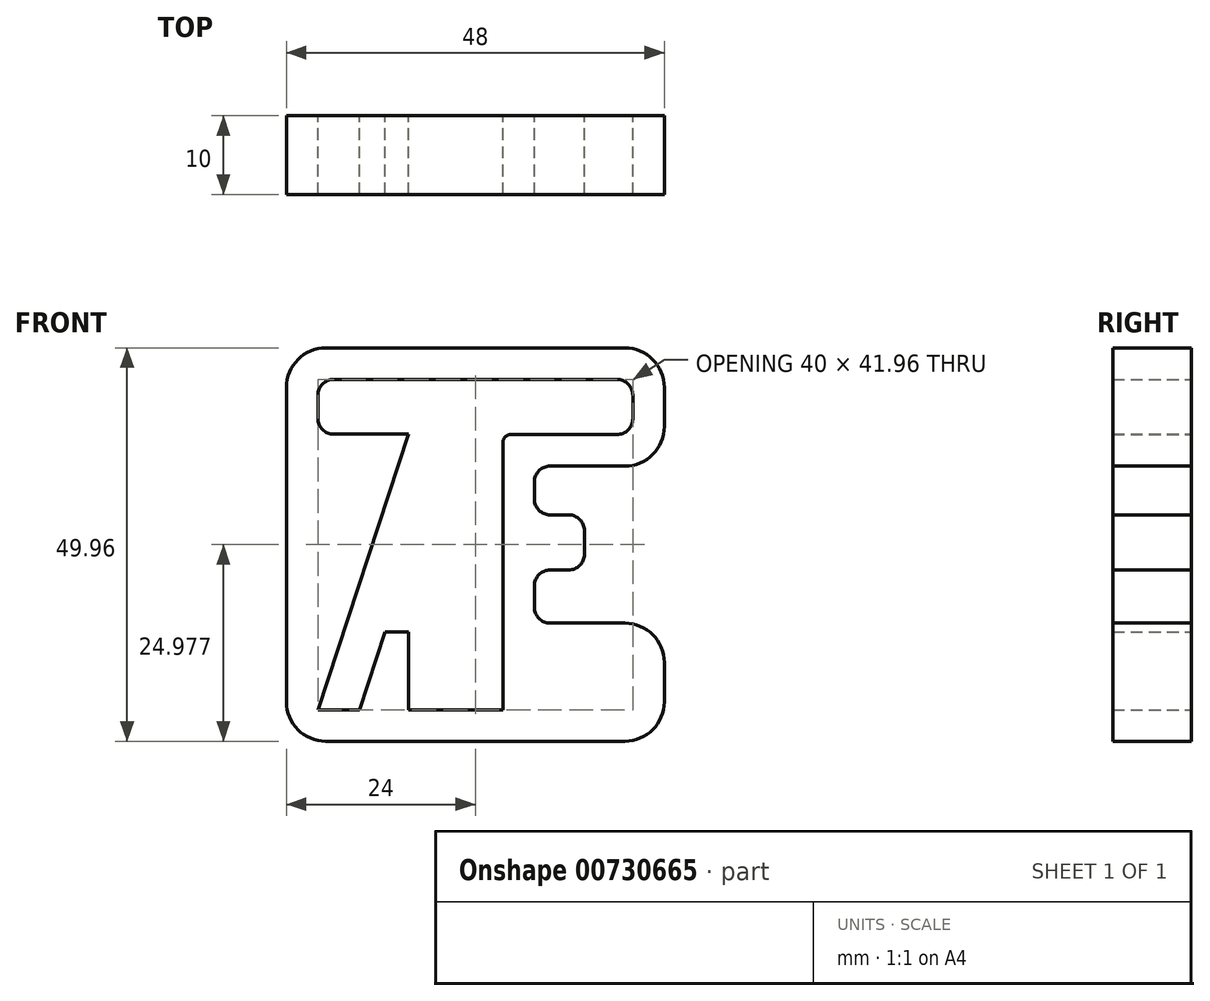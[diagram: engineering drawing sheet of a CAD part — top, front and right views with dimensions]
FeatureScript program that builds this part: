
annotation { "Feature Type Name" : "Feature", "Feature Type Description" : "" }
export const myFeature = defineFeature(function(context is Context, id is Id, definition is map)
    precondition{}
    {
        {
            var Q0;
            Q0=qCreatedBy(makeId("Front.planeOp"),FACE);
            var sketch = newSketch(context, id + "F0", { "sketchPlane" : qUnion([Q0])});
            skLineSegment(sketch, "E0", {"start": v(-5, 16.18) * mm, "end": v(-16.5, -18.82) * mm});
            skLineSegment(sketch, "E1", {"start": v(-16.5, -18.82) * mm, "end": v(-11.24, -18.82) * mm});
            skLineSegment(sketch, "E2", {"start": v(-11.24, -18.82) * mm, "end": v(-8, -8.96) * mm});
            skLineSegment(sketch, "E3", {"start": v(-8, -8.96) * mm, "end": v(-5, -8.96) * mm});
            skLineSegment(sketch, "E4", {"start": v(-5, -8.96) * mm, "end": v(-5, -18.82) * mm});
            skLineSegment(sketch, "E5", {"start": v(-5, -18.82) * mm, "end": v(0, -18.82) * mm});
            skLineSegment(sketch, "E6", {"start": v(23.5, 16.14) * mm, "end": v(23.5, 23.14) * mm});
            skLineSegment(sketch, "E7", {"start": v(23.5, 23.14) * mm, "end": v(-16.5, 23.14) * mm});
            skLineSegment(sketch, "E8", {"start": v(-16.5, 23.14) * mm, "end": v(-16.5, 16.18) * mm});
            skLineSegment(sketch, "E9", {"start": v(-16.5, 16.18) * mm, "end": v(-5, 16.18) * mm});
            skLineSegment(sketch, "E10", {"start": v(23.5, 16.14) * mm, "end": v(7, 16.14) * mm});
            skLineSegment(sketch, "E11", {"start": v(7, 16.14) * mm, "end": v(7, -18.82) * mm});
            skLineSegment(sketch, "E12", {"start": v(7, -18.82) * mm, "end": v(0, -18.82) * mm});
            skLineSegment(sketch, "E13", {"start": v(27.5, 27.14) * mm, "end": v(-20.5, 27.14) * mm});
            skLineSegment(sketch, "E14", {"start": v(-20.5, 27.14) * mm, "end": v(-20.5, -22.82) * mm});
            skLineSegment(sketch, "E15", {"start": v(-20.5, -22.82) * mm, "end": v(27.5, -22.82) * mm});
            skLineSegment(sketch, "E16", {"start": v(27.5, -22.82) * mm, "end": v(27.5, -7.82) * mm});
            skLineSegment(sketch, "E17", {"start": v(27.5, -7.82) * mm, "end": v(11, -7.82) * mm});
            skLineSegment(sketch, "E18", {"start": v(11, -7.82) * mm, "end": v(11, -1.07) * mm});
            skLineSegment(sketch, "E19", {"start": v(11, -1.07) * mm, "end": v(17.35, -1.07) * mm});
            skLineSegment(sketch, "E20", {"start": v(17.35, -1.07) * mm, "end": v(17.35, 5.93) * mm});
            skLineSegment(sketch, "E21", {"start": v(17.35, 5.93) * mm, "end": v(11, 5.93) * mm});
            skLineSegment(sketch, "E22", {"start": v(11, 5.93) * mm, "end": v(11, 12.14) * mm});
            skLineSegment(sketch, "E23", {"start": v(11, 12.14) * mm, "end": v(27.5, 12.14) * mm});
            skLineSegment(sketch, "E24", {"start": v(27.5, 12.14) * mm, "end": v(27.5, 27.14) * mm});
            skSolve(sketch);
        }
        {
            var Q0;
            Q0=qSketchRegion(id+"F0",true);
            extrude(context, id + "F1", {"entities" : qUnion([Q0]), "depth" : 10 * mm, "offsetDistance" : 25 * mm});
        }
        {
            var Q0;
            Q0=makeQuery(id+"F1.opExtrude","SWEPT_EDGE",EDGE,{"disambiguationData":[OSD([sQuery(id+"F0.wireOp",EDGE,"E7"),sQuery(id+"F0.wireOp",EDGE,"E8")])]});
            var Q1;
            Q1=makeQuery(id+"F1.opExtrude","SWEPT_EDGE",EDGE,{"disambiguationData":[OSD([sQuery(id+"F0.wireOp",EDGE,"E8"),sQuery(id+"F0.wireOp",EDGE,"E9")])]});
            var Q2;
            Q2=makeQuery(id+"F1.opExtrude","SWEPT_EDGE",EDGE,{"disambiguationData":[OSD([sQuery(id+"F0.wireOp",EDGE,"E6"),sQuery(id+"F0.wireOp",EDGE,"E7")])]});
            var Q3;
            Q3=makeQuery(id+"F1.opExtrude","SWEPT_EDGE",EDGE,{"disambiguationData":[OSD([sQuery(id+"F0.wireOp",EDGE,"E6"),sQuery(id+"F0.wireOp",EDGE,"E10")])]});
            fillet(context, id + "F2", {"entities" : qUnion([Q0, Q1, Q2, Q3]), "radius" : 2 * mm, "tangentPropagation" : true, "allowEdgeOverflow" : false});
        }
        {
            var Q0;
            Q0=makeQuery(id+"F1.opExtrude","SWEPT_EDGE",EDGE,{"disambiguationData":[OSD([sQuery(id+"F0.wireOp",EDGE,"E13"),sQuery(id+"F0.wireOp",EDGE,"E14")])]});
            var Q1;
            Q1=makeQuery(id+"F1.opExtrude","SWEPT_EDGE",EDGE,{"disambiguationData":[OSD([sQuery(id+"F0.wireOp",EDGE,"E13"),sQuery(id+"F0.wireOp",EDGE,"E24")])]});
            var Q2;
            Q2=makeQuery(id+"F1.opExtrude","SWEPT_EDGE",EDGE,{"disambiguationData":[OSD([sQuery(id+"F0.wireOp",EDGE,"E23"),sQuery(id+"F0.wireOp",EDGE,"E24")])]});
            var Q3;
            Q3=makeQuery(id+"F1.opExtrude","SWEPT_EDGE",EDGE,{"disambiguationData":[OSD([sQuery(id+"F0.wireOp",EDGE,"E14"),sQuery(id+"F0.wireOp",EDGE,"E15")])]});
            var Q4;
            Q4=makeQuery(id+"F1.opExtrude","SWEPT_EDGE",EDGE,{"disambiguationData":[OSD([sQuery(id+"F0.wireOp",EDGE,"E15"),sQuery(id+"F0.wireOp",EDGE,"E16")])]});
            var Q5;
            Q5=makeQuery(id+"F1.opExtrude","SWEPT_EDGE",EDGE,{"disambiguationData":[OSD([sQuery(id+"F0.wireOp",EDGE,"E16"),sQuery(id+"F0.wireOp",EDGE,"E17")])]});
            fillet(context, id + "F3", {"entities" : qUnion([Q0, Q1, Q2, Q3, Q4, Q5]), "radius" : 5 * mm, "tangentPropagation" : true, "allowEdgeOverflow" : false});
        }
        {
            var Q0;
            Q0=makeQuery(id+"F1.opExtrude","SWEPT_EDGE",EDGE,{"disambiguationData":[OSD([sQuery(id+"F0.wireOp",EDGE,"E22"),sQuery(id+"F0.wireOp",EDGE,"E23")])]});
            var Q1;
            Q1=makeQuery(id+"F1.opExtrude","SWEPT_EDGE",EDGE,{"disambiguationData":[OSD([sQuery(id+"F0.wireOp",EDGE,"E21"),sQuery(id+"F0.wireOp",EDGE,"E22")])]});
            var Q2;
            Q2=makeQuery(id+"F1.opExtrude","SWEPT_EDGE",EDGE,{"disambiguationData":[OSD([sQuery(id+"F0.wireOp",EDGE,"E20"),sQuery(id+"F0.wireOp",EDGE,"E21")])]});
            var Q3;
            Q3=makeQuery(id+"F1.opExtrude","SWEPT_EDGE",EDGE,{"disambiguationData":[OSD([sQuery(id+"F0.wireOp",EDGE,"E19"),sQuery(id+"F0.wireOp",EDGE,"E20")])]});
            var Q4;
            Q4=makeQuery(id+"F1.opExtrude","SWEPT_EDGE",EDGE,{"disambiguationData":[OSD([sQuery(id+"F0.wireOp",EDGE,"E18"),sQuery(id+"F0.wireOp",EDGE,"E19")])]});
            var Q5;
            Q5=makeQuery(id+"F1.opExtrude","SWEPT_EDGE",EDGE,{"disambiguationData":[OSD([sQuery(id+"F0.wireOp",EDGE,"E17"),sQuery(id+"F0.wireOp",EDGE,"E18")])]});
            fillet(context, id + "F4", {"entities" : qUnion([Q0, Q1, Q2, Q3, Q4, Q5]), "radius" : 2 * mm, "tangentPropagation" : true, "allowEdgeOverflow" : false});
        }
        {
            var Q0;
            Q0=makeQuery(id+"F1.opExtrude","SWEPT_EDGE",EDGE,{"disambiguationData":[OSD([sQuery(id+"F0.wireOp",EDGE,"E10"),sQuery(id+"F0.wireOp",EDGE,"E11")])]});
            fillet(context, id + "F5", {"entities" : qUnion([Q0]), "radius" : 1 * mm, "tangentPropagation" : true, "allowEdgeOverflow" : false});
        }
    });
